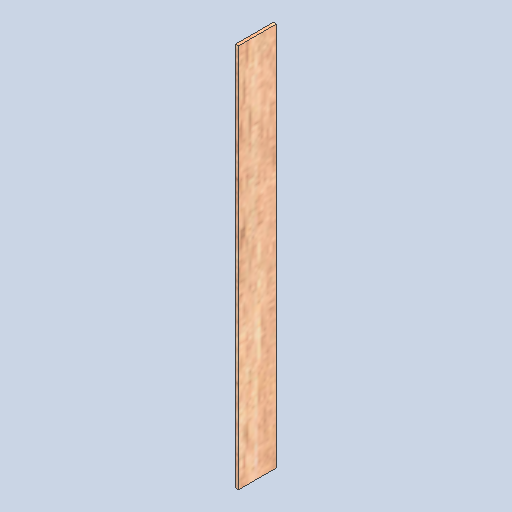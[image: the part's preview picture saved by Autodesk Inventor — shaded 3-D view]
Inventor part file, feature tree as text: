
AUTODESK INVENTOR PART (.ipt)
format: ipt  version: 2022 (Build 260153000, 153)  size: 122,368 bytes
history: native  units: in
note: dims shown in document units (in); Inventor stores cm internally (conversion verified against a paired STEP export)
features: extrude x1, sketch x1
ambient origin geometry x8: Origin, YZ Plane, XZ Plane, XY Plane, X Axis, Y Axis, Z Axis, Center Point
bodies: Solid1 (feature_tree)
feature tree (2):
  extrude  "Extrusion1"  Depth=0.5in
  sketch  "Sketch1"  dims[d0=5.1in d1=0.5in d2=0.04in d3=0.0in]
